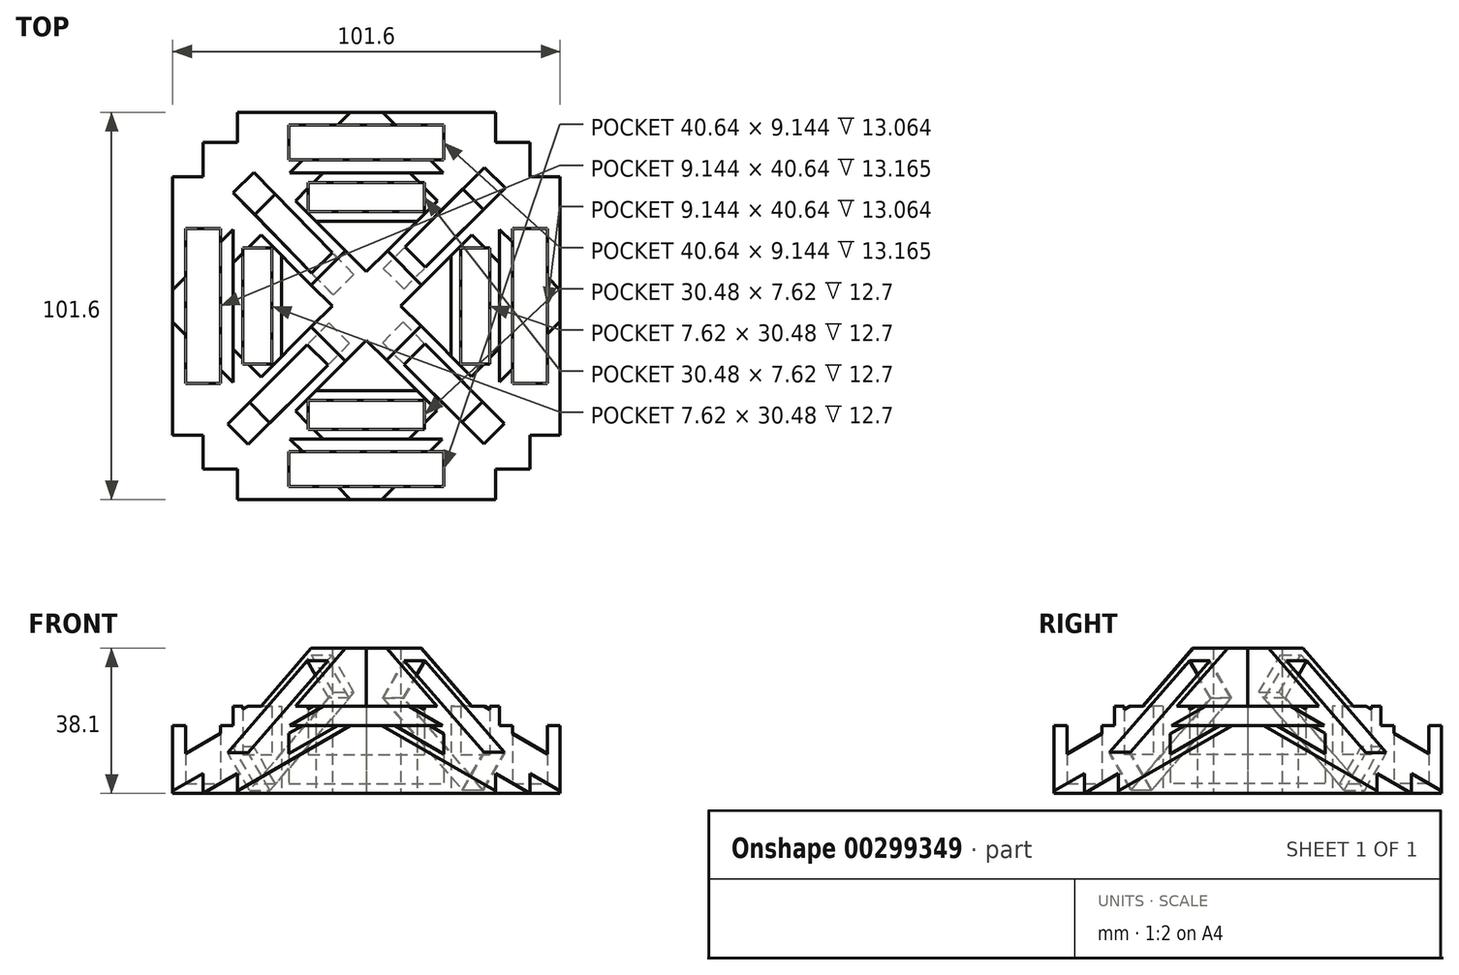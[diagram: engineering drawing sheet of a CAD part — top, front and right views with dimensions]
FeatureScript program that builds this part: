
annotation { "Feature Type Name" : "Feature", "Feature Type Description" : "" }
export const myFeature = defineFeature(function(context is Context, id is Id, definition is map)
    precondition{}
    {
        {
            var Q0;
            Q0=qCreatedBy(makeId("Top.planeOp"),FACE);
            var sketch = newSketch(context, id + "F0", { "sketchPlane" : qUnion([Q0])});
            skLineSegment(sketch, "E0.bottom", {"start": v(60.12, -50.8) * mm, "end": v(-41.48, -50.8) * mm});
            skLineSegment(sketch, "E0.top", {"start": v(60.12, 50.8) * mm, "end": v(-41.48, 50.8) * mm});
            skLineSegment(sketch, "E0.left", {"start": v(60.12, -50.8) * mm, "end": v(60.12, 50.8) * mm});
            skLineSegment(sketch, "E0.right", {"start": v(-41.48, -50.8) * mm, "end": v(-41.48, 50.8) * mm});
            skLineSegment(sketch, "E1.bottom", {"start": v(52.18, -42.86) * mm, "end": v(-33.54, -42.86) * mm, "construction": true});
            skLineSegment(sketch, "E1.top", {"start": v(52.18, 42.86) * mm, "end": v(-33.54, 42.86) * mm, "construction": true});
            skLineSegment(sketch, "E1.left", {"start": v(52.18, -42.86) * mm, "end": v(52.18, 42.86) * mm, "construction": true});
            skLineSegment(sketch, "E1.right", {"start": v(-33.54, -42.86) * mm, "end": v(-33.54, 42.86) * mm, "construction": true});
            skPoint(sketch, "E1.middle", {"position": v(9.32, 0) * mm});
            skLineSegment(sketch, "E2", {"start": v(9.32, -34.93) * mm, "end": v(9.32, -38.3) * mm, "construction": true});
            skLineSegment(sketch, "E3.bottom", {"start": v(-11, 47.43) * mm, "end": v(29.64, 47.43) * mm});
            skLineSegment(sketch, "E3.top", {"start": v(-11, 38.3) * mm, "end": v(29.64, 38.3) * mm});
            skLineSegment(sketch, "E3.left", {"start": v(-11, 47.43) * mm, "end": v(-11, 38.3) * mm});
            skLineSegment(sketch, "E3.right", {"start": v(29.64, 47.43) * mm, "end": v(29.64, 38.3) * mm});
            skLineSegment(sketch, "E4.bottom", {"start": v(-38.11, 20.32) * mm, "end": v(-28.97, 20.32) * mm});
            skLineSegment(sketch, "E4.top", {"start": v(-38.11, -20.32) * mm, "end": v(-28.97, -20.32) * mm});
            skLineSegment(sketch, "E4.left", {"start": v(-38.11, 20.32) * mm, "end": v(-38.11, -20.32) * mm});
            skLineSegment(sketch, "E4.right", {"start": v(-28.97, 20.32) * mm, "end": v(-28.97, -20.32) * mm});
            skLineSegment(sketch, "E5.bottom", {"start": v(47.61, 20.32) * mm, "end": v(56.76, 20.32) * mm});
            skLineSegment(sketch, "E5.top", {"start": v(47.61, -20.32) * mm, "end": v(56.76, -20.32) * mm});
            skLineSegment(sketch, "E5.left", {"start": v(47.61, 20.32) * mm, "end": v(47.61, -20.32) * mm});
            skLineSegment(sketch, "E5.right", {"start": v(56.76, 20.32) * mm, "end": v(56.76, -20.32) * mm});
            skLineSegment(sketch, "E6", {"start": v(-28.97, 0) * mm, "end": v(-25.6, 0) * mm, "construction": true});
            skLineSegment(sketch, "E7", {"start": v(-38.11, 0) * mm, "end": v(-41.48, 0) * mm, "construction": true});
            skLineSegment(sketch, "E8", {"start": v(9.32, -47.43) * mm, "end": v(9.32, -50.8) * mm, "construction": true});
            skLineSegment(sketch, "E9", {"start": v(47.61, 0) * mm, "end": v(44.25, 0) * mm, "construction": true});
            skLineSegment(sketch, "E10", {"start": v(56.76, 0) * mm, "end": v(60.12, 0) * mm, "construction": true});
            skLineSegment(sketch, "E11", {"start": v(9.32, 47.43) * mm, "end": v(9.32, 50.8) * mm, "construction": true});
            skLineSegment(sketch, "E12", {"start": v(9.32, 38.3) * mm, "end": v(9.32, 34.93) * mm, "construction": true});
            skLineSegment(sketch, "E13", {"start": v(-25.6, 34.93) * mm, "end": v(-25.6, -34.93) * mm});
            skLineSegment(sketch, "E14", {"start": v(44.25, 34.93) * mm, "end": v(44.25, -34.93) * mm});
            skLineSegment(sketch, "E15", {"start": v(-25.6, -34.93) * mm, "end": v(44.25, -34.93) * mm});
            skLineSegment(sketch, "E16", {"start": v(-25.6, 34.93) * mm, "end": v(44.25, 34.93) * mm});
            skLineSegment(sketch, "E17", {"start": v(-11, -38.3) * mm, "end": v(29.64, -38.3) * mm});
            skLineSegment(sketch, "E18", {"start": v(-11, -47.43) * mm, "end": v(29.64, -47.43) * mm});
            skLineSegment(sketch, "E19", {"start": v(29.64, -47.43) * mm, "end": v(29.64, -38.3) * mm});
            skLineSegment(sketch, "E20", {"start": v(-11, -47.43) * mm, "end": v(-11, -38.3) * mm});
            skLineSegment(sketch, "E21.bottom", {"start": v(-5.92, -24.77) * mm, "end": v(24.56, -24.77) * mm});
            skLineSegment(sketch, "E21.top", {"start": v(-5.92, -32.39) * mm, "end": v(24.56, -32.39) * mm});
            skLineSegment(sketch, "E21.left", {"start": v(-5.92, -24.77) * mm, "end": v(-5.92, -32.39) * mm});
            skLineSegment(sketch, "E21.right", {"start": v(24.56, -24.77) * mm, "end": v(24.56, -32.39) * mm});
            skLineSegment(sketch, "E22.bottom", {"start": v(34.09, 15.24) * mm, "end": v(41.7, 15.24) * mm});
            skLineSegment(sketch, "E22.top", {"start": v(34.09, -15.24) * mm, "end": v(41.7, -15.24) * mm});
            skLineSegment(sketch, "E22.left", {"start": v(34.09, 15.24) * mm, "end": v(34.09, -15.24) * mm});
            skLineSegment(sketch, "E22.right", {"start": v(41.7, 15.24) * mm, "end": v(41.7, -15.24) * mm});
            skLineSegment(sketch, "E23.bottom", {"start": v(-5.92, 32.39) * mm, "end": v(24.56, 32.39) * mm});
            skLineSegment(sketch, "E23.top", {"start": v(-5.92, 24.77) * mm, "end": v(24.56, 24.77) * mm});
            skLineSegment(sketch, "E23.left", {"start": v(-5.92, 32.39) * mm, "end": v(-5.92, 24.77) * mm});
            skLineSegment(sketch, "E23.right", {"start": v(24.56, 32.39) * mm, "end": v(24.56, 24.77) * mm});
            skLineSegment(sketch, "E24.bottom", {"start": v(-23.06, 15.24) * mm, "end": v(-15.44, 15.24) * mm});
            skLineSegment(sketch, "E24.top", {"start": v(-23.06, -15.24) * mm, "end": v(-15.44, -15.24) * mm});
            skLineSegment(sketch, "E24.left", {"start": v(-23.06, 15.24) * mm, "end": v(-23.06, -15.24) * mm});
            skLineSegment(sketch, "E24.right", {"start": v(-15.44, 15.24) * mm, "end": v(-15.44, -15.24) * mm});
            skLineSegment(sketch, "E25", {"start": v(9.32, -32.39) * mm, "end": v(9.32, -34.93) * mm, "construction": true});
            skLineSegment(sketch, "E26", {"start": v(-23.06, 0) * mm, "end": v(-25.6, 0) * mm, "construction": true});
            skLineSegment(sketch, "E27", {"start": v(9.32, 32.39) * mm, "end": v(9.32, 34.93) * mm, "construction": true});
            skLineSegment(sketch, "E28", {"start": v(41.7, 0) * mm, "end": v(44.25, 0) * mm, "construction": true});
            skLineSegment(sketch, "E29", {"start": v(9.32, 24.77) * mm, "end": v(9.32, 22.23) * mm, "construction": true});
            skLineSegment(sketch, "E30", {"start": v(31.55, -0.55) * mm, "end": v(34.09, -0.55) * mm, "construction": true});
            skLineSegment(sketch, "E31", {"start": v(-12.9, 0) * mm, "end": v(-15.44, 0) * mm, "construction": true});
            skLineSegment(sketch, "E32", {"start": v(9.32, -22.22) * mm, "end": v(9.32, -24.77) * mm, "construction": true});
            skLineSegment(sketch, "E33", {"start": v(-3.92, 22.22) * mm, "end": v(22.57, 22.22) * mm});
            skLineSegment(sketch, "E34", {"start": v(31.55, 13.24) * mm, "end": v(31.55, -13.24) * mm});
            skLineSegment(sketch, "E35", {"start": v(-12.9, -13.24) * mm, "end": v(-12.9, 13.24) * mm});
            skLineSegment(sketch, "E36", {"start": v(-3.92, -22.23) * mm, "end": v(22.57, -22.22) * mm});
            skLineSegment(sketch, "E37", {"start": v(-41.48, 50.8) * mm, "end": v(60.12, -50.8) * mm, "construction": true});
            skLineSegment(sketch, "E38", {"start": v(-41.48, -50.8) * mm, "end": v(60.12, 50.8) * mm, "construction": true});
            skLineSegment(sketch, "E39", {"start": v(52.18, -33.88) * mm, "end": v(60.12, -33.88) * mm});
            skLineSegment(sketch, "E40", {"start": v(43.2, -42.86) * mm, "end": v(43.2, -50.8) * mm});
            skLineSegment(sketch, "E41", {"start": v(-24.56, -42.86) * mm, "end": v(-24.56, -50.8) * mm});
            skLineSegment(sketch, "E42", {"start": v(-33.54, -33.88) * mm, "end": v(-41.48, -33.88) * mm});
            skLineSegment(sketch, "E43", {"start": v(43.2, 42.86) * mm, "end": v(43.2, 50.8) * mm});
            skLineSegment(sketch, "E44", {"start": v(52.18, 33.88) * mm, "end": v(60.12, 33.88) * mm});
            skLineSegment(sketch, "E45", {"start": v(-24.56, 42.86) * mm, "end": v(-24.56, 50.8) * mm});
            skLineSegment(sketch, "E46", {"start": v(-33.54, 33.88) * mm, "end": v(-41.48, 33.88) * mm});
            skLineSegment(sketch, "E47", {"start": v(-41.13, -41.47) * mm, "end": v(-32.15, -50.45) * mm});
            skLineSegment(sketch, "E48", {"start": v(51.14, 50.8) * mm, "end": v(60.12, 41.82) * mm});
            skLineSegment(sketch, "E49", {"start": v(60.12, 41.82) * mm, "end": v(-32.15, -50.45) * mm});
            skLineSegment(sketch, "E50", {"start": v(51.14, 50.8) * mm, "end": v(-41.13, -41.47) * mm});
            skLineSegment(sketch, "E51", {"start": v(-41.48, 41.82) * mm, "end": v(51.14, -50.8) * mm});
            skLineSegment(sketch, "E52", {"start": v(-32.5, 50.8) * mm, "end": v(60.12, -41.82) * mm});
            skLineSegment(sketch, "E53", {"start": v(51.14, -50.8) * mm, "end": v(60.12, -41.82) * mm});
            skLineSegment(sketch, "E54", {"start": v(-41.48, 41.82) * mm, "end": v(-32.5, 50.8) * mm});
            skLineSegment(sketch, "E55", {"start": v(-33.54, -33.88) * mm, "end": v(-33.54, -42.86) * mm});
            skLineSegment(sketch, "E56", {"start": v(-24.56, -42.86) * mm, "end": v(-33.54, -42.86) * mm});
            skLineSegment(sketch, "E57", {"start": v(43.2, -42.86) * mm, "end": v(52.18, -42.86) * mm});
            skLineSegment(sketch, "E58", {"start": v(52.18, -33.88) * mm, "end": v(52.18, -42.86) * mm});
            skLineSegment(sketch, "E59", {"start": v(52.18, 42.86) * mm, "end": v(52.18, 33.88) * mm});
            skLineSegment(sketch, "E60", {"start": v(43.2, 42.86) * mm, "end": v(52.18, 42.86) * mm});
            skLineSegment(sketch, "E61", {"start": v(-33.54, 42.86) * mm, "end": v(-33.54, 33.88) * mm});
            skLineSegment(sketch, "E62", {"start": v(-33.54, 42.86) * mm, "end": v(-24.56, 42.86) * mm});
            skSolve(sketch);
        }
        {
            var Q0;
            {var subQ8=sQuery(id+"F0.wireOp",EDGE,"E50");var subQ10=makeQuery(id+"F0.imprint","IMPRINT",VERTEX,{"derivedFrom":subQ8});Q0=makeQuery(id+"F0.imprint","IMPRINT",FACE,{"disambiguationData":[TD([[makeQuery(id+"F0.imprint","IMPRINT",EDGE,{"disambiguationData":[TD([[subQ10,1.0]])],"derivedFrom":subQ8}),1.0]])]});}
            var Q1;
            {var subQ2=sQuery(id+"F0.wireOp",EDGE,"E14");var subQ4=sQuery(id+"F0.wireOp",EDGE,"E16");var subQ5=makeQuery(id+"F0.imprint","INTERSECT",VERTEX,{"derivedFrom":[subQ2,subQ4]});Q1=makeQuery(id+"F0.imprint","IMPRINT",FACE,{"disambiguationData":[TD([[makeQuery(id+"F0.imprint","IMPRINT",EDGE,{"disambiguationData":[TD([[subQ5,-1.0]])],"derivedFrom":subQ2}),-1.0]])]});}
            var Q2;
            {var subQ5=sQuery(id+"F0.wireOp",EDGE,"E16");var subQ6=sQuery(id+"F0.wireOp",EDGE,"E13");var subQ7=makeQuery(id+"F0.imprint","INTERSECT",VERTEX,{"derivedFrom":[subQ6,subQ5]});Q2=makeQuery(id+"F0.imprint","IMPRINT",FACE,{"disambiguationData":[TD([[makeQuery(id+"F0.imprint","IMPRINT",EDGE,{"disambiguationData":[TD([[subQ7,-1.0]])],"derivedFrom":subQ6}),1.0]])]});}
            var Q3;
            {var subQ6=sQuery(id+"F0.wireOp",EDGE,"E15");var subQ7=sQuery(id+"F0.wireOp",EDGE,"E14");var subQ8=makeQuery(id+"F0.imprint","INTERSECT",VERTEX,{"derivedFrom":[subQ7,subQ6]});Q3=makeQuery(id+"F0.imprint","IMPRINT",FACE,{"disambiguationData":[TD([[makeQuery(id+"F0.imprint","IMPRINT",EDGE,{"disambiguationData":[TD([[subQ8,1.0]])],"derivedFrom":subQ7}),-1.0]])]});}
            var Q4;
            {var subQ2=sQuery(id+"F0.wireOp",EDGE,"E14");var subQ4=sQuery(id+"F0.wireOp",EDGE,"E16");var subQ5=makeQuery(id+"F0.imprint","INTERSECT",VERTEX,{"derivedFrom":[subQ2,subQ4]});Q4=makeQuery(id+"F0.imprint","IMPRINT",FACE,{"disambiguationData":[TD([[makeQuery(id+"F0.imprint","IMPRINT",EDGE,{"disambiguationData":[TD([[subQ5,-1.0]])],"derivedFrom":subQ2}),-1.0]])]});}
            var Q5;
            {var subQ8=sQuery(id+"F0.wireOp",EDGE,"E50");var subQ10=makeQuery(id+"F0.imprint","IMPRINT",VERTEX,{"derivedFrom":subQ8});Q5=makeQuery(id+"F0.imprint","IMPRINT",FACE,{"disambiguationData":[TD([[makeQuery(id+"F0.imprint","IMPRINT",EDGE,{"disambiguationData":[TD([[subQ10,1.0]])],"derivedFrom":subQ8}),1.0]])]});}
            var Q6;
            {var subQ0=sQuery(id+"F0.wireOp",EDGE,"E52");var subQ1=sQuery(id+"F0.wireOp",EDGE,"E49");var subQ2=makeQuery(id+"F0.imprint","INTERSECT",VERTEX,{"derivedFrom":[subQ1,subQ0]});Q6=makeQuery(id+"F0.imprint","IMPRINT",FACE,{"disambiguationData":[TD([[makeQuery(id+"F0.imprint","IMPRINT",EDGE,{"disambiguationData":[TD([[subQ2,-1.0]])],"derivedFrom":subQ1}),-1.0]])]});}
            var Q7;
            {var subQ4=sQuery(id+"F0.wireOp",EDGE,"E15");var subQ5=sQuery(id+"F0.wireOp",EDGE,"E13");var subQ6=makeQuery(id+"F0.imprint","INTERSECT",VERTEX,{"derivedFrom":[subQ5,subQ4]});Q7=makeQuery(id+"F0.imprint","IMPRINT",FACE,{"disambiguationData":[TD([[makeQuery(id+"F0.imprint","IMPRINT",EDGE,{"disambiguationData":[TD([[subQ6,1.0]])],"derivedFrom":subQ5}),1.0]])]});}
            var Q8;
            {var subQ0=sQuery(id+"F0.wireOp",EDGE,"E57");Q8=makeQuery(id+"F0.imprint","IMPRINT",FACE,{"disambiguationData":[TD([[makeQuery(id+"F0.imprint","IMPRINT",EDGE,{"derivedFrom":subQ0}),1.0]])]});}
            var Q9;
            {var subQ6=sQuery(id+"F0.wireOp",EDGE,"E55");Q9=makeQuery(id+"F0.imprint","IMPRINT",FACE,{"disambiguationData":[TD([[makeQuery(id+"F0.imprint","IMPRINT",EDGE,{"derivedFrom":subQ6}),1.0]])]});}
            var Q10;
            {var subQ6=sQuery(id+"F0.wireOp",EDGE,"E61");Q10=makeQuery(id+"F0.imprint","IMPRINT",FACE,{"disambiguationData":[TD([[makeQuery(id+"F0.imprint","IMPRINT",EDGE,{"derivedFrom":subQ6}),1.0]])]});}
            var Q11;
            {var subQ0=sQuery(id+"F0.wireOp",EDGE,"E59");Q11=makeQuery(id+"F0.imprint","IMPRINT",FACE,{"disambiguationData":[TD([[makeQuery(id+"F0.imprint","IMPRINT",EDGE,{"derivedFrom":subQ0}),-1.0]])]});}
            extrude(context, id + "F1", {"entities" : qUnion([Q0, Q1, Q2, Q3, Q4, Q5, Q6, Q7, Q8, Q9, Q10, Q11]), "depth" : 44.45 * mm});
        }
        {
            var Q0;
            Q0=makeQuery(id+"F0.imprint","IMPRINT",FACE,{"disambiguationData":[TD([[makeQuery(id+"F0.imprint","IMPRINT",EDGE,{"derivedFrom":sQuery(id+"F0.wireOp",EDGE,"E21.bottom")}),-1.0]])]});
            var Q1;
            Q1=makeQuery(id+"F0.imprint","IMPRINT",FACE,{"disambiguationData":[TD([[makeQuery(id+"F0.imprint","IMPRINT",EDGE,{"derivedFrom":sQuery(id+"F0.wireOp",EDGE,"E21.bottom")}),1.0]])]});
            var Q2;
            Q2=makeQuery(id+"F0.imprint","IMPRINT",FACE,{"disambiguationData":[TD([[makeQuery(id+"F0.imprint","IMPRINT",EDGE,{"derivedFrom":sQuery(id+"F0.wireOp",EDGE,"E22.bottom")}),-1.0]])]});
            var Q3;
            Q3=makeQuery(id+"F0.imprint","IMPRINT",FACE,{"disambiguationData":[TD([[makeQuery(id+"F0.imprint","IMPRINT",EDGE,{"derivedFrom":sQuery(id+"F0.wireOp",EDGE,"E22.bottom")}),1.0]])]});
            var Q4;
            Q4=makeQuery(id+"F0.imprint","IMPRINT",FACE,{"disambiguationData":[TD([[makeQuery(id+"F0.imprint","IMPRINT",EDGE,{"derivedFrom":sQuery(id+"F0.wireOp",EDGE,"E23.bottom")}),-1.0]])]});
            var Q5;
            Q5=makeQuery(id+"F0.imprint","IMPRINT",FACE,{"disambiguationData":[TD([[makeQuery(id+"F0.imprint","IMPRINT",EDGE,{"derivedFrom":sQuery(id+"F0.wireOp",EDGE,"E23.bottom")}),1.0]])]});
            var Q6;
            Q6=makeQuery(id+"F0.imprint","IMPRINT",FACE,{"disambiguationData":[TD([[makeQuery(id+"F0.imprint","IMPRINT",EDGE,{"derivedFrom":sQuery(id+"F0.wireOp",EDGE,"E24.bottom")}),-1.0]])]});
            var Q7;
            Q7=makeQuery(id+"F0.imprint","IMPRINT",FACE,{"disambiguationData":[TD([[makeQuery(id+"F0.imprint","IMPRINT",EDGE,{"derivedFrom":sQuery(id+"F0.wireOp",EDGE,"E24.bottom")}),1.0]])]});
            extrude(context, id + "F2", {"entities" : qUnion([Q0, Q1, Q2, Q3, Q4, Q5, Q6, Q7]), "operationType" : NewBodyOperationType.ADD, "depth" : 22.86 * mm});
        }
        {
            var Q0;
            Q0=makeQuery(id+"F0.imprint","IMPRINT",FACE,{"disambiguationData":[TD([[makeQuery(id+"F0.imprint","IMPRINT",EDGE,{"derivedFrom":sQuery(id+"F0.wireOp",EDGE,"E4.bottom")}),-1.0]])]});
            var Q1;
            Q1=makeQuery(id+"F0.imprint","IMPRINT",FACE,{"disambiguationData":[TD([[makeQuery(id+"F0.imprint","IMPRINT",EDGE,{"derivedFrom":sQuery(id+"F0.wireOp",EDGE,"E4.bottom")}),1.0]])]});
            var Q2;
            Q2=makeQuery(id+"F0.imprint","IMPRINT",FACE,{"disambiguationData":[TD([[makeQuery(id+"F0.imprint","IMPRINT",EDGE,{"derivedFrom":sQuery(id+"F0.wireOp",EDGE,"E17")}),-1.0]])]});
            var Q3;
            Q3=makeQuery(id+"F0.imprint","IMPRINT",FACE,{"disambiguationData":[TD([[makeQuery(id+"F0.imprint","IMPRINT",EDGE,{"derivedFrom":sQuery(id+"F0.wireOp",EDGE,"E17")}),1.0]])]});
            var Q4;
            Q4=makeQuery(id+"F0.imprint","IMPRINT",FACE,{"disambiguationData":[TD([[makeQuery(id+"F0.imprint","IMPRINT",EDGE,{"derivedFrom":sQuery(id+"F0.wireOp",EDGE,"E5.bottom")}),-1.0]])]});
            var Q5;
            Q5=makeQuery(id+"F0.imprint","IMPRINT",FACE,{"disambiguationData":[TD([[makeQuery(id+"F0.imprint","IMPRINT",EDGE,{"derivedFrom":sQuery(id+"F0.wireOp",EDGE,"E5.bottom")}),1.0]])]});
            var Q6;
            Q6=makeQuery(id+"F0.imprint","IMPRINT",FACE,{"disambiguationData":[TD([[makeQuery(id+"F0.imprint","IMPRINT",EDGE,{"derivedFrom":sQuery(id+"F0.wireOp",EDGE,"E3.bottom")}),-1.0]])]});
            var Q7;
            Q7=makeQuery(id+"F0.imprint","IMPRINT",FACE,{"disambiguationData":[TD([[makeQuery(id+"F0.imprint","IMPRINT",EDGE,{"derivedFrom":sQuery(id+"F0.wireOp",EDGE,"E3.bottom")}),1.0]])]});
            extrude(context, id + "F3", {"entities" : qUnion([Q0, Q1, Q2, Q3, Q4, Q5, Q6, Q7]), "operationType" : NewBodyOperationType.ADD, "depth" : 17.78 * mm});
        }
        {
            var Q0;
            {var subQ0=sQuery(id+"F0.wireOp",EDGE,"E51");var subQ1=makeQuery(id+"F0.imprint","INTERSECT",VERTEX,{"derivedFrom":[sQuery(id+"F0.wireOp",EDGE,"E35"),subQ0]});var subQ2=makeQuery(id+"F0.imprint","INTERSECT",VERTEX,{"derivedFrom":[sQuery(id+"F0.wireOp",EDGE,"E13"),subQ0]});Q0=makeQuery(id+"F1.opExtrude","SWEPT_FACE",FACE,{"disambiguationData":[OSD([subQ0]),TDD([makeQuery(id+"F0.imprint","IMPRINT",EDGE,{"disambiguationData":[TD([[subQ2,1.0]])],"derivedFrom":subQ0}),makeQuery(id+"F0.imprint","IMPRINT",EDGE,{"disambiguationData":[TD([[subQ1,1.0]])],"derivedFrom":subQ0}),makeQuery(id+"F0.imprint","IMPRINT",EDGE,{"disambiguationData":[TD([[subQ1,-1.0]])],"derivedFrom":subQ0})])]});}
            var sketch = newSketch(context, id + "F4", { "sketchPlane" : qUnion([Q0])});
            skLineSegment(sketch, "E63", {"start": v(0.24, 44.45) * mm, "end": v(-54.03, 44.45) * mm});
            skLineSegment(sketch, "E64", {"start": v(-54.03, 44.45) * mm, "end": v(-54.03, 0) * mm});
            skLineSegment(sketch, "E65", {"start": v(-54.03, 0) * mm, "end": v(0.24, 44.45) * mm});
            skLineSegment(sketch, "E66", {"start": v(12.59, 44.45) * mm, "end": v(67.2, 44.45) * mm});
            skLineSegment(sketch, "E67", {"start": v(67.2, 44.45) * mm, "end": v(67.2, 0) * mm});
            skLineSegment(sketch, "E68", {"start": v(67.2, 0) * mm, "end": v(12.59, 44.45) * mm});
            skSolve(sketch);
        }
        {
            var Q0;
            Q0=qSketchRegion(id+"F4",true);
            extrude(context, id + "F5", {"entities" : qUnion([Q0]), "operationType" : NewBodyOperationType.REMOVE, "endBound" : BoundingType.SYMMETRIC, "depth" : 89.4 * mm});
        }
        {
            var Q0;
            {var subQ0=sQuery(id+"F0.wireOp",EDGE,"E49");var subQ1=makeQuery(id+"F0.imprint","INTERSECT",VERTEX,{"derivedFrom":[sQuery(id+"F0.wireOp",EDGE,"E34"),subQ0]});var subQ3=makeQuery(id+"F0.imprint","INTERSECT",VERTEX,{"derivedFrom":[sQuery(id+"F0.wireOp",EDGE,"E44"),subQ0]});Q0=makeQuery(id+"F1.opExtrude","SWEPT_FACE",FACE,{"disambiguationData":[OSD([subQ0]),TDD([makeQuery(id+"F0.imprint","IMPRINT",EDGE,{"disambiguationData":[TD([[subQ3,1.0]])],"derivedFrom":subQ0}),makeQuery(id+"F0.imprint","IMPRINT",EDGE,{"disambiguationData":[TD([[subQ3,-1.0]])],"derivedFrom":subQ0}),makeQuery(id+"F0.imprint","IMPRINT",EDGE,{"disambiguationData":[TD([[subQ1,1.0]])],"derivedFrom":subQ0}),makeQuery(id+"F0.imprint","IMPRINT",EDGE,{"disambiguationData":[TD([[subQ1,-1.0]])],"derivedFrom":subQ0})])]});}
            var sketch = newSketch(context, id + "F6", { "sketchPlane" : qUnion([Q0])});
            skLineSegment(sketch, "E69", {"start": v(-54.03, 44.45) * mm, "end": v(12.94, 44.45) * mm});
            skLineSegment(sketch, "E70", {"start": v(0.24, 44.45) * mm, "end": v(-54.03, 44.45) * mm});
            skLineSegment(sketch, "E71", {"start": v(-54.03, 44.45) * mm, "end": v(-54.03, 0) * mm});
            skLineSegment(sketch, "E72", {"start": v(-54.03, 0) * mm, "end": v(0.24, 44.45) * mm});
            skLineSegment(sketch, "E73", {"start": v(0.24, 44.45) * mm, "end": v(0.24, -6.35) * mm, "construction": true});
            skLineSegment(sketch, "E74", {"start": v(12.94, 44.45) * mm, "end": v(12.94, -6.35) * mm, "construction": true});
            skLineSegment(sketch, "E75", {"start": v(12.94, 44.45) * mm, "end": v(67.2, 44.45) * mm});
            skLineSegment(sketch, "E76", {"start": v(67.2, 44.45) * mm, "end": v(67.2, 0) * mm});
            skLineSegment(sketch, "E77", {"start": v(12.94, 44.45) * mm, "end": v(67.2, 0) * mm});
            skSolve(sketch);
        }
        {
            var Q0;
            Q0=qSketchRegion(id+"F6",true);
            extrude(context, id + "F7", {"entities" : qUnion([Q0]), "operationType" : NewBodyOperationType.REMOVE, "endBound" : BoundingType.SYMMETRIC, "oppositeDirection" : true, "depth" : 95 * mm});
        }
        {
            var Q0;
            Q0=makeQuery(id+"F7.boolean.opBoolean","COPY",FACE,{"derivedFrom":makeQuery(id+"F7.opExtrude","SWEPT_FACE",FACE,{"disambiguationData":[OSD([sQuery(id+"F6.wireOp",EDGE,"E72")])]})});
            var sketch = newSketch(context, id + "F8", { "sketchPlane" : qUnion([Q0])});
            skLineSegment(sketch, "E78", {"start": v(-7.06, -26.13) * mm, "end": v(16.25, 4) * mm});
            skLineSegment(sketch, "E79", {"start": v(16.25, 4) * mm, "end": v(10.22, 8.67) * mm});
            skLineSegment(sketch, "E80", {"start": v(10.22, 8.67) * mm, "end": v(-13.09, -21.47) * mm});
            skLineSegment(sketch, "E81", {"start": v(-13.09, -21.47) * mm, "end": v(-7.06, -26.13) * mm});
            skLineSegment(sketch, "E82", {"start": v(-8.14, -27.52) * mm, "end": v(-6.13, -29.07) * mm, "construction": true});
            skLineSegment(sketch, "E83", {"start": v(-18.35, -28.27) * mm, "end": v(-20.36, -26.71) * mm, "construction": true});
            skSolve(sketch);
        }
        {
            var Q0;
            Q0=makeQuery(id+"F8.imprint","IMPRINT",FACE,{"disambiguationData":[TD([[makeQuery(id+"F8.imprint","IMPRINT",EDGE,{"derivedFrom":sQuery(id+"F8.wireOp",EDGE,"E78")}),1.0]])]});
            var Q1;
            Q1=makeQuery(id+"F8.imprint","IMPRINT",FACE,{"disambiguationData":[TD([[makeQuery(id+"F8.imprint","IMPRINT",EDGE,{"derivedFrom":sQuery(id+"F8.wireOp",EDGE,"8V8QPYWx-bIMz-7pxV-4DD2-aRToVMcrJPwS")}),1.0]])]});
            extrude(context, id + "F9", {"entities" : qUnion([Q0, Q1]), "operationType" : NewBodyOperationType.REMOVE, "oppositeDirection" : true, "depth" : 12.7 * mm});
        }
        {
            var Q0;
            Q0=makeQuery(id+"F5.boolean.opBoolean","COPY",FACE,{"derivedFrom":makeQuery(id+"F5.opExtrude","SWEPT_FACE",FACE,{"disambiguationData":[OSD([sQuery(id+"F4.wireOp",EDGE,"E65")])]})});
            var sketch = newSketch(context, id + "F10", { "sketchPlane" : qUnion([Q0])});
            skLineSegment(sketch, "E84", {"start": v(-11.54, 19.6) * mm, "end": v(11.46, -10.77) * mm});
            skLineSegment(sketch, "E85", {"start": v(11.46, -10.77) * mm, "end": v(17.53, -6.17) * mm});
            skLineSegment(sketch, "E86", {"start": v(17.53, -6.17) * mm, "end": v(-5.46, 24.2) * mm});
            skLineSegment(sketch, "E87", {"start": v(-5.46, 24.2) * mm, "end": v(-11.54, 19.6) * mm});
            skLineSegment(sketch, "E88", {"start": v(-3.02, 20.98) * mm, "end": v(-0.94, 22.44) * mm, "construction": true});
            skLineSegment(sketch, "E89", {"start": v(-6.25, 12.62) * mm, "end": v(-8.27, 11.08) * mm, "construction": true});
            skSolve(sketch);
        }
        {
            var Q0;
            Q0=qSketchRegion(id+"F10",true);
            extrude(context, id + "F11", {"entities" : qUnion([Q0]), "operationType" : NewBodyOperationType.REMOVE, "oppositeDirection" : true, "depth" : 12.7 * mm});
        }
        {
            var Q0;
            Q0=makeQuery(id+"F5.boolean.opBoolean","COPY",FACE,{"derivedFrom":makeQuery(id+"F5.opExtrude","SWEPT_FACE",FACE,{"disambiguationData":[OSD([sQuery(id+"F4.wireOp",EDGE,"E68")])]})});
            var sketch = newSketch(context, id + "F12", { "sketchPlane" : qUnion([Q0])});
            skLineSegment(sketch, "E90", {"start": v(0.3, 4.1) * mm, "end": v(23.66, -26) * mm});
            skLineSegment(sketch, "E91", {"start": v(23.66, -26) * mm, "end": v(29.68, -21.33) * mm});
            skLineSegment(sketch, "E92", {"start": v(29.68, -21.33) * mm, "end": v(6.33, 8.77) * mm});
            skLineSegment(sketch, "E93", {"start": v(6.33, 8.77) * mm, "end": v(0.3, 4.1) * mm});
            skLineSegment(sketch, "E94", {"start": v(13.13, 0) * mm, "end": v(15.16, 1.57) * mm, "construction": true});
            skLineSegment(sketch, "E95", {"start": v(3.5, 0) * mm, "end": v(1.47, -1.57) * mm, "construction": true});
            skSolve(sketch);
        }
        {
            var Q0;
            Q0=qSketchRegion(id+"F12",true);
            extrude(context, id + "F13", {"entities" : qUnion([Q0]), "operationType" : NewBodyOperationType.REMOVE, "oppositeDirection" : true, "depth" : 12.7 * mm});
        }
        {
            var Q0;
            Q0=makeQuery(id+"F7.boolean.opBoolean","COPY",FACE,{"derivedFrom":makeQuery(id+"F7.opExtrude","SWEPT_FACE",FACE,{"disambiguationData":[OSD([sQuery(id+"F6.wireOp",EDGE,"E77")])]})});
            var sketch = newSketch(context, id + "F14", { "sketchPlane" : qUnion([Q0])});
            skLineSegment(sketch, "E96", {"start": v(0.42, -4) * mm, "end": v(23.73, 26.13) * mm});
            skLineSegment(sketch, "E97", {"start": v(29.76, 21.47) * mm, "end": v(23.73, 26.13) * mm});
            skLineSegment(sketch, "E98", {"start": v(29.76, 21.47) * mm, "end": v(6.44, -8.67) * mm});
            skLineSegment(sketch, "E99", {"start": v(0.42, -4) * mm, "end": v(6.44, -8.67) * mm});
            skLineSegment(sketch, "E100", {"start": v(59.68, 76.76) * mm, "end": v(61.7, 75.2) * mm, "construction": true});
            skLineSegment(sketch, "E101", {"start": v(35.02, 28.27) * mm, "end": v(37.03, 26.71) * mm, "construction": true});
            skSolve(sketch);
        }
        {
            var Q0;
            Q0=makeQuery(id+"F14.imprint","IMPRINT",FACE,{"disambiguationData":[TD([[makeQuery(id+"F14.imprint","IMPRINT",EDGE,{"derivedFrom":sQuery(id+"F14.wireOp",EDGE,"PXSmDIBN-2tml-Z0vo-LpKr-TCqjQjuChPah")}),1.0]])]});
            var Q1;
            Q1=makeQuery(id+"F14.imprint","IMPRINT",FACE,{"disambiguationData":[TD([[makeQuery(id+"F14.imprint","IMPRINT",EDGE,{"derivedFrom":sQuery(id+"F14.wireOp",EDGE,"E96")}),-1.0]])]});
            extrude(context, id + "F15", {"entities" : qUnion([Q0, Q1]), "operationType" : NewBodyOperationType.REMOVE, "oppositeDirection" : true, "depth" : 12.7 * mm});
        }
        {
            var Q0;
            Q0=makeQuery(id+"F0.imprint","IMPRINT",FACE,{"disambiguationData":[TD([[makeQuery(id+"F0.imprint","IMPRINT",EDGE,{"derivedFrom":sQuery(id+"F0.wireOp",EDGE,"E3.bottom")}),-1.0]])]});
            var Q1;
            Q1=makeQuery(id+"F0.imprint","IMPRINT",FACE,{"disambiguationData":[TD([[makeQuery(id+"F0.imprint","IMPRINT",EDGE,{"derivedFrom":sQuery(id+"F0.wireOp",EDGE,"E4.bottom")}),-1.0]])]});
            var Q2;
            Q2=makeQuery(id+"F0.imprint","IMPRINT",FACE,{"disambiguationData":[TD([[makeQuery(id+"F0.imprint","IMPRINT",EDGE,{"derivedFrom":sQuery(id+"F0.wireOp",EDGE,"E5.bottom")}),-1.0]])]});
            var Q3;
            Q3=makeQuery(id+"F0.imprint","IMPRINT",FACE,{"disambiguationData":[TD([[makeQuery(id+"F0.imprint","IMPRINT",EDGE,{"derivedFrom":sQuery(id+"F0.wireOp",EDGE,"hdSJAShs-a5JY-Bjx8-EBj0-h0MvsXi7NyDv.bottom")}),-1.0]])]});
            var Q4;
            Q4=makeQuery(id+"F0.imprint","IMPRINT",FACE,{"disambiguationData":[TD([[makeQuery(id+"F0.imprint","IMPRINT",EDGE,{"derivedFrom":sQuery(id+"F0.wireOp",EDGE,"E17")}),-1.0]])]});
            extrude(context, id + "F16", {"entities" : qUnion([Q0, Q1, Q2, Q3, Q4]), "operationType" : NewBodyOperationType.REMOVE, "depth" : 54.86 * mm, "hasSecondDirection" : true, "secondDirectionOppositeDirection" : false, "secondDirectionDepth" : 2.54 * mm});
        }
        {
            var Q0;
            Q0=makeQuery(id+"F0.imprint","IMPRINT",FACE,{"disambiguationData":[TD([[makeQuery(id+"F0.imprint","IMPRINT",EDGE,{"derivedFrom":sQuery(id+"F0.wireOp",EDGE,"E21.bottom")}),-1.0]])]});
            var Q1;
            Q1=makeQuery(id+"F0.imprint","IMPRINT",FACE,{"disambiguationData":[TD([[makeQuery(id+"F0.imprint","IMPRINT",EDGE,{"derivedFrom":sQuery(id+"F0.wireOp",EDGE,"E22.bottom")}),-1.0]])]});
            var Q2;
            Q2=makeQuery(id+"F0.imprint","IMPRINT",FACE,{"disambiguationData":[TD([[makeQuery(id+"F0.imprint","IMPRINT",EDGE,{"derivedFrom":sQuery(id+"F0.wireOp",EDGE,"E23.bottom")}),-1.0]])]});
            var Q3;
            Q3=makeQuery(id+"F0.imprint","IMPRINT",FACE,{"disambiguationData":[TD([[makeQuery(id+"F0.imprint","IMPRINT",EDGE,{"derivedFrom":sQuery(id+"F0.wireOp",EDGE,"E24.bottom")}),-1.0]])]});
            extrude(context, id + "F17", {"entities" : qUnion([Q0, Q1, Q2, Q3]), "operationType" : NewBodyOperationType.REMOVE, "depth" : 50.8 * mm, "hasSecondDirection" : true, "secondDirectionOppositeDirection" : false, "secondDirectionDepth" : 10.16 * mm});
        }
        {
            var Q0;
            Q0=qCreatedBy(makeId("Front.planeOp"),FACE);
            var sketch = newSketch(context, id + "F18", { "sketchPlane" : qUnion([Q0])});
            skLineSegment(sketch, "E102.bottom", {"start": v(-7.33, 44.45) * mm, "end": v(30.77, 44.45) * mm});
            skLineSegment(sketch, "E102.top", {"start": v(-7.33, 38.1) * mm, "end": v(30.77, 38.1) * mm});
            skLineSegment(sketch, "E102.left", {"start": v(-7.33, 44.45) * mm, "end": v(-7.33, 38.1) * mm});
            skLineSegment(sketch, "E102.right", {"start": v(30.77, 44.45) * mm, "end": v(30.77, 38.1) * mm});
            skSolve(sketch);
        }
        {
            var Q0;
            Q0=makeQuery(id+"F18.imprint","IMPRINT",FACE,{"disambiguationData":[TD([[makeQuery(id+"F18.imprint","IMPRINT",EDGE,{"derivedFrom":sQuery(id+"F18.wireOp",EDGE,"E102.bottom")}),-1.0]])]});
            extrude(context, id + "F19", {"entities" : qUnion([Q0]), "operationType" : NewBodyOperationType.REMOVE, "endBound" : BoundingType.SYMMETRIC, "oppositeDirection" : true, "depth" : 32.5 * mm});
        }
    });
